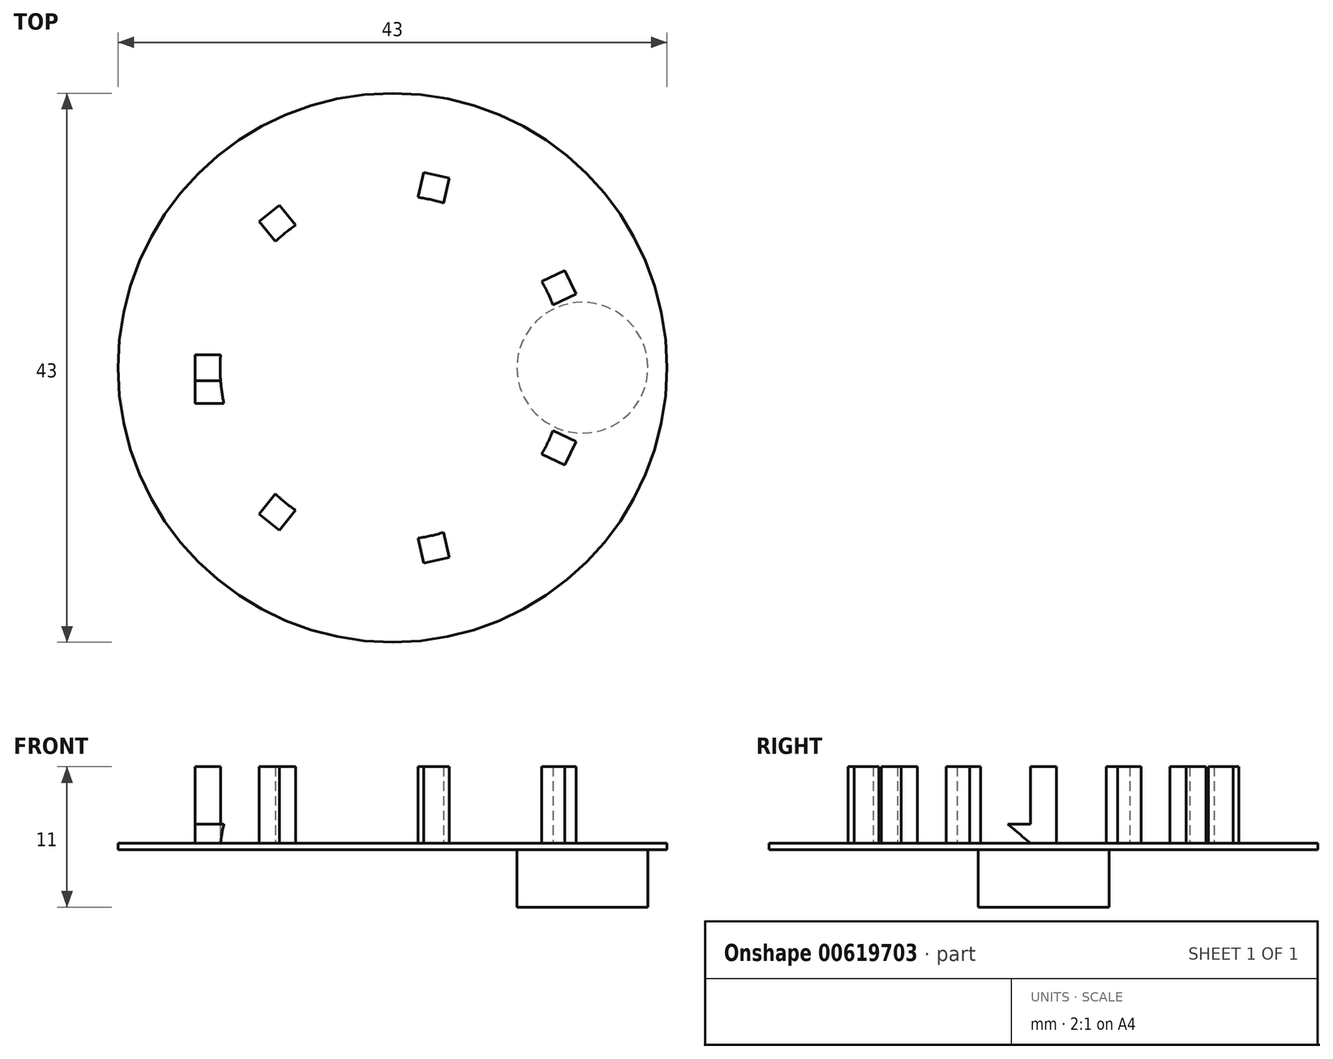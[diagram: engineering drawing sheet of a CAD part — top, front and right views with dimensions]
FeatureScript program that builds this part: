
annotation { "Feature Type Name" : "Feature", "Feature Type Description" : "" }
export const myFeature = defineFeature(function(context is Context, id is Id, definition is map)
    precondition{}
    {
        {
            var Q0;
            Q0=qCreatedBy(makeId("Top.planeOp"),FACE);
            var sketch = newSketch(context, id + "F0", { "sketchPlane" : qUnion([Q0])});
            skCircle(sketch, "E0", {"center": v(0, 0) * mm, "radius": 13.5 * mm});
            skCircle(sketch, "E1", {"center": v(0, 0) * mm, "radius": 21.5 * mm});
            skSolve(sketch);
        }
        {
            var Q0;
            Q0=makeQuery(id+"F0.imprint","IMPRINT",FACE,{"disambiguationData":[TD([[makeQuery(id+"F0.imprint","IMPRINT",EDGE,{"derivedFrom":sQuery(id+"F0.wireOp",EDGE,"E0")}),-1.0]])]});
            var Q1;
            Q1=makeQuery(id+"F0.imprint","IMPRINT",FACE,{"disambiguationData":[TD([[makeQuery(id+"F0.imprint","IMPRINT",EDGE,{"derivedFrom":sQuery(id+"F0.wireOp",EDGE,"E0")}),1.0]])]});
            extrude(context, id + "F1", {"entities" : qUnion([Q0, Q1]), "depth" : 5 * mm, "offsetDistance" : 25 * mm});
        }
        {
            var Q0;
            Q0=makeQuery(id+"F1.opExtrude","CAP_FACE",FACE,{"disambiguationData":[OSD([sQuery(id+"F0.wireOp",EDGE,"E1")])],"isStart":false});
            var sketch = newSketch(context, id + "F2", { "sketchPlane" : qUnion([Q0])});
            skCircle(sketch, "E2", {"center": v(0, 0) * mm, "radius": 13.5 * mm, "construction": true});
            skLineSegment(sketch, "E3.bottom", {"start": v(-13.46, 1.02) * mm, "end": v(-15.46, 1.02) * mm});
            skLineSegment(sketch, "E3.top", {"start": v(-13.46, -1.02) * mm, "end": v(-15.46, -1.02) * mm});
            skLineSegment(sketch, "E3.right", {"start": v(-15.46, 1.02) * mm, "end": v(-15.46, -1.02) * mm});
            skPoint(sketch, "E3.middle", {"position": v(-14.46, 0) * mm});
            skArc(sketch, "E4", {"start": v(-13.46, 1.02) * mm, "mid": v(-13.5, 0) * mm, "end": v(-13.46, -1.02) * mm});
            skArc(sketch, "E5.1.0", {"start": v(-9.19, -9.89) * mm, "mid": v(-8.42, -10.55) * mm, "end": v(-7.6, -11.16) * mm});
            skLineSegment(sketch, "E5.1.1", {"start": v(-10.44, -11.45) * mm, "end": v(-8.84, -12.72) * mm});
            skLineSegment(sketch, "E5.1.2", {"start": v(-7.6, -11.16) * mm, "end": v(-8.84, -12.72) * mm});
            skLineSegment(sketch, "E5.1.3", {"start": v(-9.19, -9.89) * mm, "end": v(-10.44, -11.45) * mm});
            skPoint(sketch, "E5.1.4", {"position": v(-9.02, -11.3) * mm});
            skArc(sketch, "E5.2.0", {"start": v(2, -13.35) * mm, "mid": v(3, -13.16) * mm, "end": v(3.99, -12.9) * mm});
            skLineSegment(sketch, "E5.2.1", {"start": v(2.45, -15.3) * mm, "end": v(4.43, -14.85) * mm});
            skLineSegment(sketch, "E5.2.2", {"start": v(3.99, -12.9) * mm, "end": v(4.43, -14.85) * mm});
            skLineSegment(sketch, "E5.2.3", {"start": v(2, -13.35) * mm, "end": v(2.45, -15.3) * mm});
            skPoint(sketch, "E5.2.4", {"position": v(3.22, -14.1) * mm});
            skArc(sketch, "E5.3.0", {"start": v(11.69, -6.76) * mm, "mid": v(12.16, -5.86) * mm, "end": v(12.57, -4.92) * mm});
            skLineSegment(sketch, "E5.3.1", {"start": v(13.49, -7.63) * mm, "end": v(14.37, -5.8) * mm});
            skLineSegment(sketch, "E5.3.2", {"start": v(12.57, -4.92) * mm, "end": v(14.37, -5.8) * mm});
            skLineSegment(sketch, "E5.3.3", {"start": v(11.69, -6.76) * mm, "end": v(13.49, -7.63) * mm});
            skPoint(sketch, "E5.3.4", {"position": v(13.03, -6.27) * mm});
            skArc(sketch, "E5.4.0", {"start": v(12.57, 4.92) * mm, "mid": v(12.16, 5.86) * mm, "end": v(11.69, 6.76) * mm});
            skLineSegment(sketch, "E5.4.1", {"start": v(14.37, 5.8) * mm, "end": v(13.49, 7.63) * mm});
            skLineSegment(sketch, "E5.4.2", {"start": v(11.69, 6.76) * mm, "end": v(13.49, 7.63) * mm});
            skLineSegment(sketch, "E5.4.3", {"start": v(12.57, 4.92) * mm, "end": v(14.37, 5.8) * mm});
            skPoint(sketch, "E5.4.4", {"position": v(13.03, 6.27) * mm});
            skArc(sketch, "E5.5.0", {"start": v(3.99, 12.9) * mm, "mid": v(3, 13.16) * mm, "end": v(2, 13.35) * mm});
            skLineSegment(sketch, "E5.5.1", {"start": v(4.43, 14.85) * mm, "end": v(2.45, 15.3) * mm});
            skLineSegment(sketch, "E5.5.2", {"start": v(2, 13.35) * mm, "end": v(2.45, 15.3) * mm});
            skLineSegment(sketch, "E5.5.3", {"start": v(3.99, 12.9) * mm, "end": v(4.43, 14.85) * mm});
            skPoint(sketch, "E5.5.4", {"position": v(3.22, 14.1) * mm});
            skArc(sketch, "E5.6.0", {"start": v(-7.6, 11.16) * mm, "mid": v(-8.42, 10.55) * mm, "end": v(-9.19, 9.89) * mm});
            skLineSegment(sketch, "E5.6.1", {"start": v(-8.84, 12.72) * mm, "end": v(-10.44, 11.45) * mm});
            skLineSegment(sketch, "E5.6.2", {"start": v(-9.19, 9.89) * mm, "end": v(-10.44, 11.45) * mm});
            skLineSegment(sketch, "E5.6.3", {"start": v(-7.6, 11.16) * mm, "end": v(-8.84, 12.72) * mm});
            skPoint(sketch, "E5.6.4", {"position": v(-9.02, 11.3) * mm});
            skSolve(sketch);
        }
        {
            var Q0;
            Q0=qSketchRegion(id+"F2",true);
            extrude(context, id + "F3", {"entities" : qUnion([Q0]), "operationType" : NewBodyOperationType.ADD, "depth" : 6 * mm, "offsetDistance" : 25 * mm});
        }
        {
            var Q0;
            Q0=makeQuery(id+"F1.opExtrude","CAP_FACE",FACE,{"disambiguationData":[OSD([sQuery(id+"F0.wireOp",EDGE,"E1")])],"isStart":true});
            var sketch = newSketch(context, id + "F4", { "sketchPlane" : qUnion([Q0])});
            skCircle(sketch, "E6", {"center": v(-14.88, 0) * mm, "radius": 5.12 * mm});
            skCircle(sketch, "E7.MirrorC", {"center": v(14.88, 0) * mm, "radius": 5.12 * mm});
            skCircle(sketch, "E8", {"center": v(0, 0) * mm, "radius": 13.5 * mm, "construction": true});
            skSolve(sketch);
        }
        {
            var Q0;
            Q0=makeQuery(id+"F4.imprint","IMPRINT",FACE,{"disambiguationData":[TD([[makeQuery(id+"F4.imprint","IMPRINT",EDGE,{"derivedFrom":sQuery(id+"F4.wireOp",EDGE,"E6")}),1.0]])]});
            var Q1;
            Q1=makeQuery(id+"F4.imprint","IMPRINT",FACE,{"disambiguationData":[TD([[makeQuery(id+"F4.imprint","IMPRINT",EDGE,{"derivedFrom":sQuery(id+"F4.wireOp",EDGE,"E7.MirrorC")}),-1.0]])]});
            extrude(context, id + "F5", {"entities" : qUnion([Q0, Q1]), "operationType" : NewBodyOperationType.REMOVE, "oppositeDirection" : true, "depth" : 4.5 * mm, "offsetDistance" : 25 * mm});
        }
        {
            var Q0;
            Q0=makeQuery(id+"F3.opExtrude","SWEPT_FACE",FACE,{"disambiguationData":[OSD([sQuery(id+"F2.wireOp",EDGE,"E3.right")])]});
            var sketch = newSketch(context, id + "F6", { "sketchPlane" : qUnion([Q0])});
            skLineSegment(sketch, "E9", {"start": v(1.02, 5) * mm, "end": v(2.8, 6.5) * mm});
            skLineSegment(sketch, "E10", {"start": v(2.8, 6.5) * mm, "end": v(1.02, 6.5) * mm});
            skSolve(sketch);
        }
        {
            var Q0;
            {var subQ0=sQuery(id+"F6.wireOp",EDGE,"E9");Q0=makeQuery(id+"F6.imprint","IMPRINT",FACE,{"disambiguationData":[TD([[makeQuery(id+"F6.imprint","IMPRINT",EDGE,{"derivedFrom":subQ0}),1.0]])]});}
            var Q1;
            Q1=makeQuery(id+"F3.opExtrude","SWEPT_FACE",FACE,{"disambiguationData":[OSD([sQuery(id+"F2.wireOp",EDGE,"E4")])]});
            extrude(context, id + "F7", {"entities" : qUnion([Q0]), "operationType" : NewBodyOperationType.ADD, "endBound" : BoundingType.UP_TO_SURFACE, "oppositeDirection" : true, "depth" : 25 * mm, "endBoundEntityFace" : qUnion([Q1]), "offsetDistance" : 25 * mm});
        }
    });
